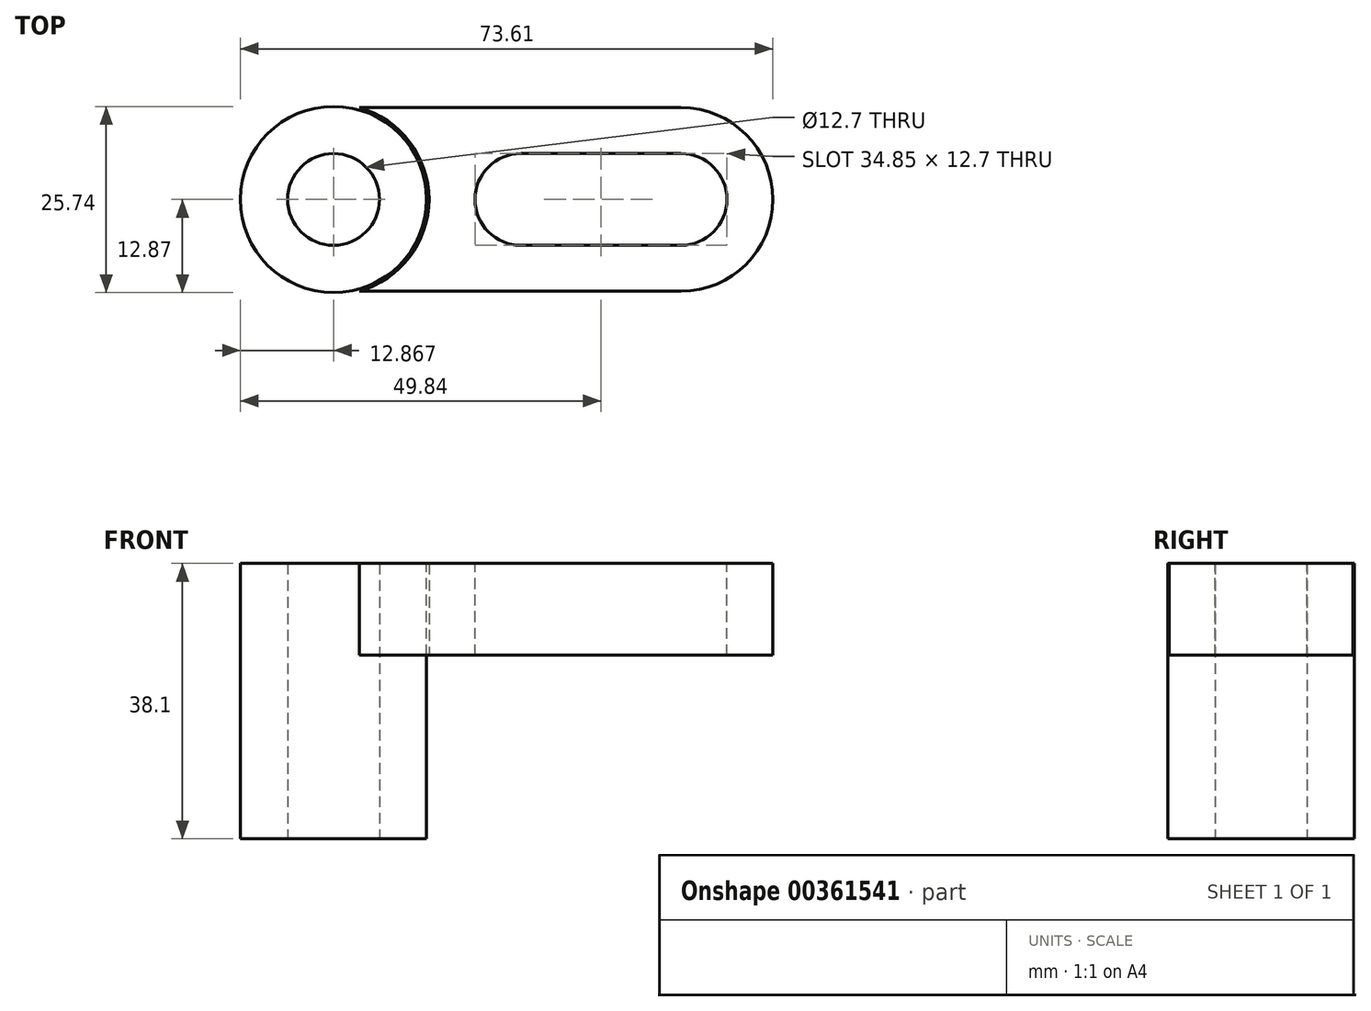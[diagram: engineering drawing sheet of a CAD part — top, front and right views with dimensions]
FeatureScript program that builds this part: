
annotation { "Feature Type Name" : "Feature", "Feature Type Description" : "" }
export const myFeature = defineFeature(function(context is Context, id is Id, definition is map)
    precondition{}
    {
        {
            var Q0;
            Q0=qCreatedBy(makeId("Top.planeOp"),FACE);
            var sketch = newSketch(context, id + "F0", { "sketchPlane" : qUnion([Q0])});
            skLineSegment(sketch, "E0.bottom", {"start": v(7.83, 25.4) * mm, "end": v(64.98, 25.4) * mm});
            skLineSegment(sketch, "E0.top", {"start": v(7.83, 0) * mm, "end": v(64.98, 0) * mm});
            skLineSegment(sketch, "E0.left", {"start": v(7.83, 25.4) * mm, "end": v(7.83, 0) * mm});
            skLineSegment(sketch, "E0.right", {"start": v(64.98, 25.4) * mm, "end": v(64.98, 0) * mm});
            skArc(sketch, "E1", {"start": v(7.83, 0) * mm, "mid": v(17.44, 12.7) * mm, "end": v(7.83, 25.4) * mm});
            skSolve(sketch);
        }
        {
            var Q0;
            Q0=makeQuery(id+"F0.imprint","IMPRINT",FACE,{"disambiguationData":[TD([[makeQuery(id+"F0.imprint","IMPRINT",EDGE,{"derivedFrom":sQuery(id+"F0.wireOp",EDGE,"E0.bottom")}),-1.0]])]});
            extrude(context, id + "F1", {"entities" : qUnion([Q0]), "depth" : 12.7 * mm});
        }
        {
            var Q0;
            Q0=makeQuery(id+"F1.opExtrude","CAP_FACE",FACE,{"disambiguationData":[OSD([sQuery(id+"F0.wireOp",EDGE,"E0.bottom"),sQuery(id+"F0.wireOp",EDGE,"E0.top"),sQuery(id+"F0.wireOp",EDGE,"E0.right"),sQuery(id+"F0.wireOp",EDGE,"E1")])],"isStart":false});
            var sketch = newSketch(context, id + "F2", { "sketchPlane" : qUnion([Q0])});
            skCircle(sketch, "E2", {"center": v(30.14, 12.7) * mm, "radius": 6.35 * mm});
            skCircle(sketch, "E3", {"center": v(52.28, 12.7) * mm, "radius": 6.35 * mm});
            skLineSegment(sketch, "E4", {"start": v(30.14, 19.05) * mm, "end": v(52.28, 19.05) * mm});
            skLineSegment(sketch, "E5", {"start": v(52.28, 6.35) * mm, "end": v(30.14, 6.35) * mm});
            skSolve(sketch);
        }
        {
            var Q0;
            {var subQ0=sQuery(id+"F2.wireOp",EDGE,"E2");var subQ1=makeQuery(id+"F2.imprint","INTERSECT",VERTEX,{"derivedFrom":[subQ0,sQuery(id+"F2.wireOp",EDGE,"E4")]});Q0=makeQuery(id+"F2.imprint","IMPRINT",FACE,{"disambiguationData":[TD([[makeQuery(id+"F2.imprint","IMPRINT",EDGE,{"disambiguationData":[TD([[subQ1,-1.0]])],"derivedFrom":subQ0}),1.0]])]});}
            var Q1;
            {var subQ0=sQuery(id+"F2.wireOp",EDGE,"E3");var subQ1=makeQuery(id+"F2.imprint","INTERSECT",VERTEX,{"derivedFrom":[subQ0,sQuery(id+"F2.wireOp",EDGE,"E4")]});Q1=makeQuery(id+"F2.imprint","IMPRINT",FACE,{"disambiguationData":[TD([[makeQuery(id+"F2.imprint","IMPRINT",EDGE,{"disambiguationData":[TD([[subQ1,-1.0]])],"derivedFrom":subQ0}),1.0]])]});}
            var Q2;
            {var subQ0=sQuery(id+"F2.wireOp",EDGE,"E4");Q2=makeQuery(id+"F2.imprint","IMPRINT",FACE,{"disambiguationData":[TD([[makeQuery(id+"F2.imprint","IMPRINT",EDGE,{"derivedFrom":subQ0}),-1.0]])]});}
            extrude(context, id + "F3", {"entities" : qUnion([Q0, Q1, Q2]), "operationType" : NewBodyOperationType.REMOVE, "oppositeDirection" : true, "depth" : 12.7 * mm});
        }
        {
            var Q0;
            Q0=makeQuery(id+"F1.opExtrude","CAP_FACE",FACE,{"disambiguationData":[OSD([sQuery(id+"F0.wireOp",EDGE,"E0.bottom"),sQuery(id+"F0.wireOp",EDGE,"E0.top"),sQuery(id+"F0.wireOp",EDGE,"E0.right"),sQuery(id+"F0.wireOp",EDGE,"E1")])],"isStart":false});
            var sketch = newSketch(context, id + "F4", { "sketchPlane" : qUnion([Q0])});
            skCircle(sketch, "E6", {"center": v(4.24, 12.7) * mm, "radius": 12.87 * mm});
            skSolve(sketch);
        }
        {
            var Q0;
            Q0 = qSketchRegion(id + "F4", true);
            extrude(context, id + "F5", {"entities" : qUnion([Q0]), "oppositeDirection" : true, "depth" : 38.1 * mm});
        }
        {
            var Q0;
            Q0=qCreatedBy(makeId("Top.planeOp"),FACE);
            var sketch = newSketch(context, id + "F6", { "sketchPlane" : qUnion([Q0])});
            skArc(sketch, "E7", {"start": v(49.52, 0) * mm, "mid": v(64.22, 12.25) * mm, "end": v(50.45, 25.54) * mm});
            skLineSegment(sketch, "E8", {"start": v(49.52, 0) * mm, "end": v(65.62, 0) * mm});
            skLineSegment(sketch, "E9", {"start": v(50.45, 25.54) * mm, "end": v(65.62, 25.54) * mm});
            skLineSegment(sketch, "E10", {"start": v(65.62, 25.54) * mm, "end": v(65.62, 0) * mm});
            skSolve(sketch);
        }
        {
            var Q0;
            {var subQ5=sQuery(id+"F6.wireOp",EDGE,"E10");Q0=makeQuery(id+"F6.imprint","IMPRINT",FACE,{"disambiguationData":[TD([[makeQuery(id+"F6.imprint","IMPRINT",EDGE,{"derivedFrom":subQ5}),-1.0]])]});}
            extrude(context, id + "F7", {"entities" : qUnion([Q0]), "operationType" : NewBodyOperationType.REMOVE, "oppositeDirection" : true, "depth" : 12.7 * mm});
        }
        {
            var Q0;
            Q0=makeQuery(id+"F5.opExtrude","CAP_FACE",FACE,{"disambiguationData":[OSD([sQuery(id+"F4.wireOp",EDGE,"E6")])],"isStart":false});
            var sketch = newSketch(context, id + "F8", { "sketchPlane" : qUnion([Q0])});
            skCircle(sketch, "E11", {"center": v(4.24, -12.7) * mm, "radius": 6.35 * mm});
            skSolve(sketch);
        }
        {
            var Q0;
            Q0=makeQuery(id+"F8.imprint","IMPRINT",FACE,{"disambiguationData":[TD([[makeQuery(id+"F8.imprint","IMPRINT",EDGE,{"derivedFrom":sQuery(id+"F8.wireOp",EDGE,"E11")}),1.0]])]});
            extrude(context, id + "F9", {"entities" : qUnion([Q0]), "operationType" : NewBodyOperationType.REMOVE, "oppositeDirection" : true, "depth" : 38.1 * mm});
        }
        {
            var Q0;
            Q0=makeQuery(id+"F1.opExtrude","CAP_FACE",FACE,{"disambiguationData":[OSD([sQuery(id+"F0.wireOp",EDGE,"E0.bottom"),sQuery(id+"F0.wireOp",EDGE,"E0.top"),sQuery(id+"F0.wireOp",EDGE,"E0.right"),sQuery(id+"F0.wireOp",EDGE,"E1")])],"isStart":false});
            var sketch = newSketch(context, id + "F10", { "sketchPlane" : qUnion([Q0])});
            skArc(sketch, "E12", {"start": v(52.28, 0) * mm, "mid": v(64.98, 12.7) * mm, "end": v(52.28, 25.4) * mm});
            skSolve(sketch);
        }
        {
            var Q0;
            {var subQ0=sQuery(id+"F10.wireOp",EDGE,"E12");var subQ1=makeQuery(id+"F1.opExtrude","CAP_EDGE",EDGE,{"disambiguationData":[OSD([sQuery(id+"F0.wireOp",EDGE,"E0.right")])],"isStart":false});var subQ2=makeQuery(id+"F10.imprint","INTERSECT",VERTEX,{"derivedFrom":[subQ1,subQ0]});Q0=makeQuery(id+"F10.imprint","IMPRINT",FACE,{"disambiguationData":[TD([[makeQuery(id+"F10.imprint","IMPRINT",EDGE,{"disambiguationData":[TD([[subQ2,-1.0]])],"derivedFrom":subQ0}),-1.0]])]});}
            var Q1;
            {var subQ0=sQuery(id+"F10.wireOp",EDGE,"E12");var subQ1=makeQuery(id+"F1.opExtrude","CAP_EDGE",EDGE,{"disambiguationData":[OSD([sQuery(id+"F0.wireOp",EDGE,"E0.right")])],"isStart":false});var subQ2=makeQuery(id+"F10.imprint","INTERSECT",VERTEX,{"derivedFrom":[subQ1,subQ0]});Q1=makeQuery(id+"F10.imprint","IMPRINT",FACE,{"disambiguationData":[TD([[makeQuery(id+"F10.imprint","IMPRINT",EDGE,{"disambiguationData":[TD([[subQ2,1.0]])],"derivedFrom":subQ0}),-1.0]])]});}
            extrude(context, id + "F11", {"entities" : qUnion([Q0, Q1]), "operationType" : NewBodyOperationType.REMOVE, "oppositeDirection" : true, "depth" : 12.7 * mm});
        }
    });
